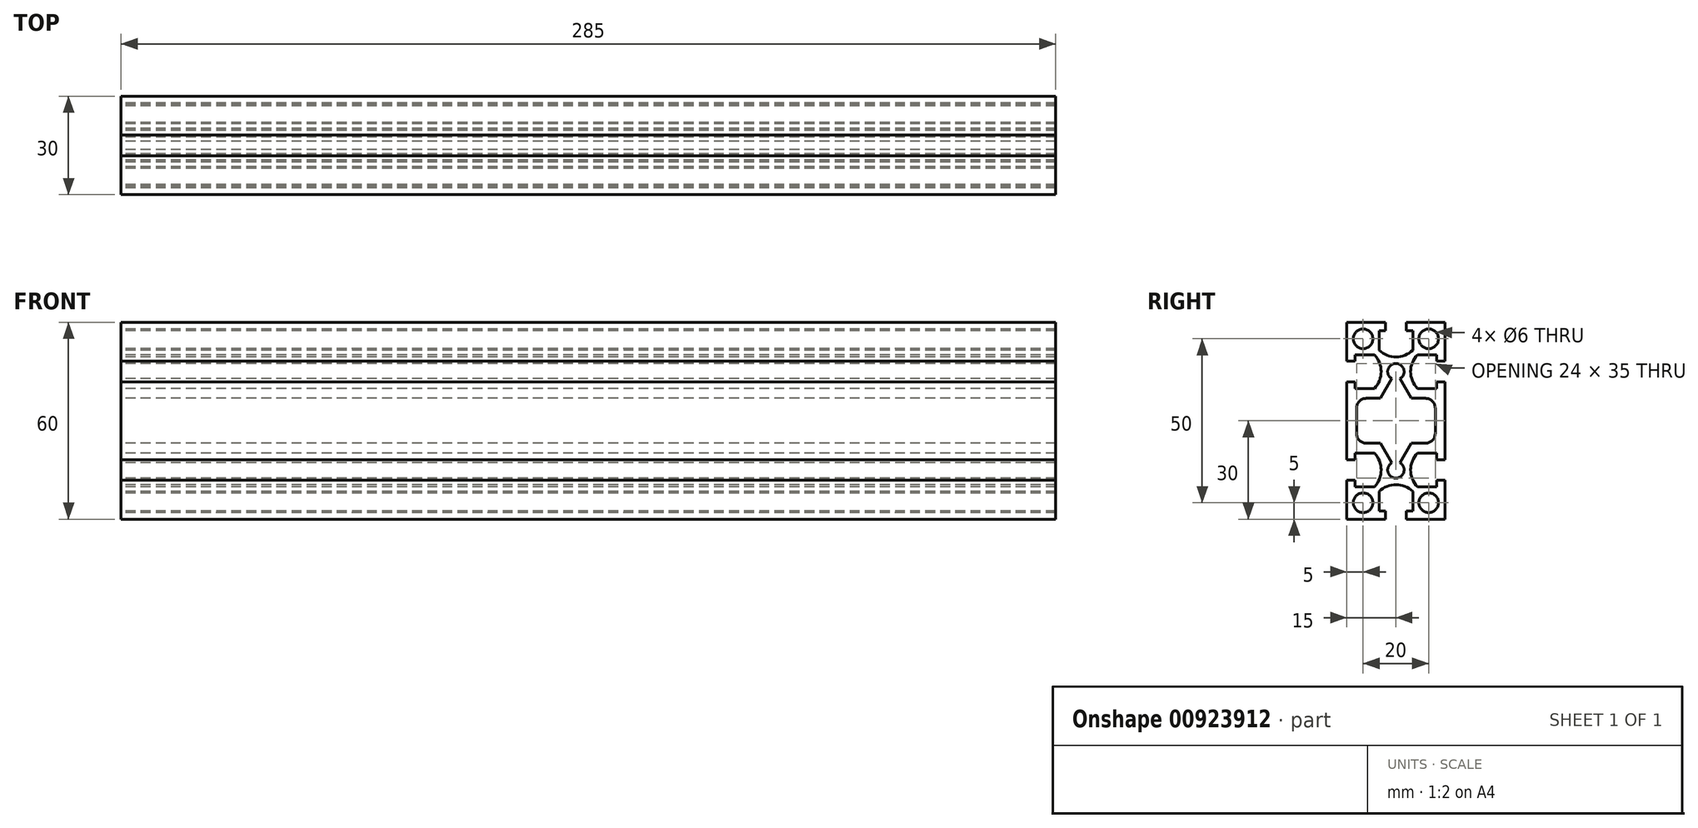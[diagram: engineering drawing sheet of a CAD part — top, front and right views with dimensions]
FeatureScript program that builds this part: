
annotation { "Feature Type Name" : "Feature", "Feature Type Description" : "" }
export const myFeature = defineFeature(function(context is Context, id is Id, definition is map)
    precondition{}
    {
        {
            var Q0;
            Q0=qCreatedBy(makeId("Right.planeOp"),FACE);
            var sketch = newSketch(context, id + "F0", { "sketchPlane" : qUnion([Q0])});
            skArc(sketch, "E0", {"start": v(-9, 6.85) * mm, "mid": v(-11.12, 5.97) * mm, "end": v(-12, 3.85) * mm});
            skLineSegment(sketch, "E1", {"start": v(-9, 6.85) * mm, "end": v(-4.7, 6.85) * mm});
            skLineSegment(sketch, "E2", {"start": v(-4.7, 6.85) * mm, "end": v(-1.25, 12.83) * mm});
            skArc(sketch, "E3", {"start": v(1.25, 12.83) * mm, "mid": v(0, 17.5) * mm, "end": v(-1.25, 12.83) * mm});
            skLineSegment(sketch, "E4", {"start": v(1.25, 12.83) * mm, "end": v(4.7, 6.85) * mm});
            skLineSegment(sketch, "E5", {"start": v(4.7, 6.85) * mm, "end": v(9, 6.85) * mm});
            skArc(sketch, "E6", {"start": v(12, 3.85) * mm, "mid": v(11.12, 5.97) * mm, "end": v(9, 6.85) * mm});
            skLineSegment(sketch, "E7", {"start": v(12, 3.85) * mm, "end": v(12, -3.85) * mm});
            skArc(sketch, "E8", {"start": v(9, -6.85) * mm, "mid": v(11.12, -5.97) * mm, "end": v(12, -3.85) * mm});
            skLineSegment(sketch, "E9", {"start": v(9, -6.85) * mm, "end": v(4.7, -6.85) * mm});
            skLineSegment(sketch, "E10", {"start": v(4.7, -6.85) * mm, "end": v(1.25, -12.83) * mm});
            skArc(sketch, "E11", {"start": v(-1.25, -12.83) * mm, "mid": v(0, -17.5) * mm, "end": v(1.25, -12.83) * mm});
            skLineSegment(sketch, "E12", {"start": v(-1.25, -12.83) * mm, "end": v(-4.7, -6.85) * mm});
            skLineSegment(sketch, "E13", {"start": v(-4.7, -6.85) * mm, "end": v(-9, -6.85) * mm});
            skArc(sketch, "E14", {"start": v(-12, -3.85) * mm, "mid": v(-11.12, -5.97) * mm, "end": v(-9, -6.85) * mm});
            skLineSegment(sketch, "E15", {"start": v(-12, -3.85) * mm, "end": v(-12, 3.85) * mm});
            skCircle(sketch, "E16", {"center": v(-10, 25) * mm, "radius": 3 * mm});
            skCircle(sketch, "E17", {"center": v(10, 25) * mm, "radius": 3 * mm});
            skCircle(sketch, "E18", {"center": v(-10, -25) * mm, "radius": 3 * mm});
            skCircle(sketch, "E19", {"center": v(10, -25) * mm, "radius": 3 * mm});
            skLineSegment(sketch, "E20", {"start": v(15, -11.85) * mm, "end": v(12.5, -11.85) * mm});
            skLineSegment(sketch, "E21", {"start": v(12.5, -11.85) * mm, "end": v(12.5, -9.85) * mm});
            skLineSegment(sketch, "E22", {"start": v(12.5, -9.85) * mm, "end": v(6.55, -9.85) * mm});
            skArc(sketch, "E23", {"start": v(6.55, -9.85) * mm, "mid": v(4.5, -15) * mm, "end": v(6.55, -20.15) * mm});
            skLineSegment(sketch, "E24", {"start": v(6.55, -20.15) * mm, "end": v(12.5, -20.15) * mm});
            skLineSegment(sketch, "E25", {"start": v(12.5, -20.15) * mm, "end": v(12.5, -18.15) * mm});
            skLineSegment(sketch, "E26", {"start": v(12.5, -18.15) * mm, "end": v(15, -18.15) * mm});
            skLineSegment(sketch, "E27", {"start": v(15, -18.15) * mm, "end": v(15, -30) * mm});
            skLineSegment(sketch, "E28", {"start": v(15, -30) * mm, "end": v(3.15, -30) * mm});
            skLineSegment(sketch, "E29", {"start": v(3.15, -30) * mm, "end": v(3.15, -27.5) * mm});
            skLineSegment(sketch, "E30", {"start": v(3.15, -27.5) * mm, "end": v(5.15, -27.5) * mm});
            skLineSegment(sketch, "E31", {"start": v(5.15, -27.5) * mm, "end": v(5.15, -21.55) * mm});
            skArc(sketch, "E32", {"start": v(5.15, -21.55) * mm, "mid": v(0, -19.5) * mm, "end": v(-5.15, -21.55) * mm});
            skLineSegment(sketch, "E33", {"start": v(-5.15, -21.55) * mm, "end": v(-5.15, -27.5) * mm});
            skLineSegment(sketch, "E34", {"start": v(-5.15, -27.5) * mm, "end": v(-3.15, -27.5) * mm});
            skLineSegment(sketch, "E35", {"start": v(-3.15, -27.5) * mm, "end": v(-3.15, -30) * mm});
            skLineSegment(sketch, "E36", {"start": v(-3.15, -30) * mm, "end": v(-15, -30) * mm});
            skLineSegment(sketch, "E37", {"start": v(-15, -30) * mm, "end": v(-15, -18.15) * mm});
            skLineSegment(sketch, "E38", {"start": v(-15, -18.15) * mm, "end": v(-12.5, -18.15) * mm});
            skLineSegment(sketch, "E39", {"start": v(-12.5, -18.15) * mm, "end": v(-12.5, -20.15) * mm});
            skLineSegment(sketch, "E40", {"start": v(-12.5, -20.15) * mm, "end": v(-6.55, -20.15) * mm});
            skArc(sketch, "E41", {"start": v(-6.55, -20.15) * mm, "mid": v(-4.5, -15) * mm, "end": v(-6.55, -9.85) * mm});
            skLineSegment(sketch, "E42", {"start": v(-6.55, -9.85) * mm, "end": v(-12.5, -9.85) * mm});
            skLineSegment(sketch, "E43", {"start": v(-12.5, -9.85) * mm, "end": v(-12.5, -11.85) * mm});
            skLineSegment(sketch, "E44", {"start": v(-12.5, -11.85) * mm, "end": v(-15, -11.85) * mm});
            skLineSegment(sketch, "E45", {"start": v(-15, -11.85) * mm, "end": v(-15, 11.85) * mm});
            skLineSegment(sketch, "E46", {"start": v(-15, 11.85) * mm, "end": v(-12.5, 11.85) * mm});
            skLineSegment(sketch, "E47", {"start": v(-12.5, 11.85) * mm, "end": v(-12.5, 9.85) * mm});
            skLineSegment(sketch, "E48", {"start": v(-12.5, 9.85) * mm, "end": v(-6.55, 9.85) * mm});
            skArc(sketch, "E49", {"start": v(-6.55, 9.85) * mm, "mid": v(-4.5, 15) * mm, "end": v(-6.55, 20.15) * mm});
            skLineSegment(sketch, "E50", {"start": v(-6.55, 20.15) * mm, "end": v(-12.5, 20.15) * mm});
            skLineSegment(sketch, "E51", {"start": v(-12.5, 20.15) * mm, "end": v(-12.5, 18.15) * mm});
            skLineSegment(sketch, "E52", {"start": v(-12.5, 18.15) * mm, "end": v(-15, 18.15) * mm});
            skLineSegment(sketch, "E53", {"start": v(-15, 18.15) * mm, "end": v(-15, 30) * mm});
            skLineSegment(sketch, "E54", {"start": v(-15, 30) * mm, "end": v(-3.15, 30) * mm});
            skLineSegment(sketch, "E55", {"start": v(-3.15, 30) * mm, "end": v(-3.15, 27.5) * mm});
            skLineSegment(sketch, "E56", {"start": v(-3.15, 27.5) * mm, "end": v(-5.15, 27.5) * mm});
            skLineSegment(sketch, "E57", {"start": v(-5.15, 27.5) * mm, "end": v(-5.15, 21.55) * mm});
            skArc(sketch, "E58", {"start": v(-5.15, 21.55) * mm, "mid": v(0, 19.5) * mm, "end": v(5.15, 21.55) * mm});
            skLineSegment(sketch, "E59", {"start": v(5.15, 21.55) * mm, "end": v(5.15, 27.5) * mm});
            skLineSegment(sketch, "E60", {"start": v(5.15, 27.5) * mm, "end": v(3.15, 27.5) * mm});
            skLineSegment(sketch, "E61", {"start": v(3.15, 27.5) * mm, "end": v(3.15, 30) * mm});
            skLineSegment(sketch, "E62", {"start": v(3.15, 30) * mm, "end": v(15, 30) * mm});
            skLineSegment(sketch, "E63", {"start": v(15, 30) * mm, "end": v(15, 18.15) * mm});
            skLineSegment(sketch, "E64", {"start": v(15, 18.15) * mm, "end": v(12.5, 18.15) * mm});
            skLineSegment(sketch, "E65", {"start": v(12.5, 18.15) * mm, "end": v(12.5, 20.15) * mm});
            skLineSegment(sketch, "E66", {"start": v(12.5, 20.15) * mm, "end": v(6.55, 20.15) * mm});
            skArc(sketch, "E67", {"start": v(6.55, 20.15) * mm, "mid": v(4.5, 15) * mm, "end": v(6.55, 9.85) * mm});
            skLineSegment(sketch, "E68", {"start": v(6.55, 9.85) * mm, "end": v(12.5, 9.85) * mm});
            skLineSegment(sketch, "E69", {"start": v(12.5, 9.85) * mm, "end": v(12.5, 11.85) * mm});
            skLineSegment(sketch, "E70", {"start": v(12.5, 11.85) * mm, "end": v(15, 11.85) * mm});
            skLineSegment(sketch, "E71", {"start": v(15, 11.85) * mm, "end": v(15, -11.85) * mm});
            skSolve(sketch);
        }
        {
            var Q0;
            Q0=qSketchRegion(id+"F0",true);
            extrude(context, id + "F1", {"entities" : qUnion([Q0]), "depth" : 285 * mm, "offsetDistance" : 25 * mm});
        }
    });
